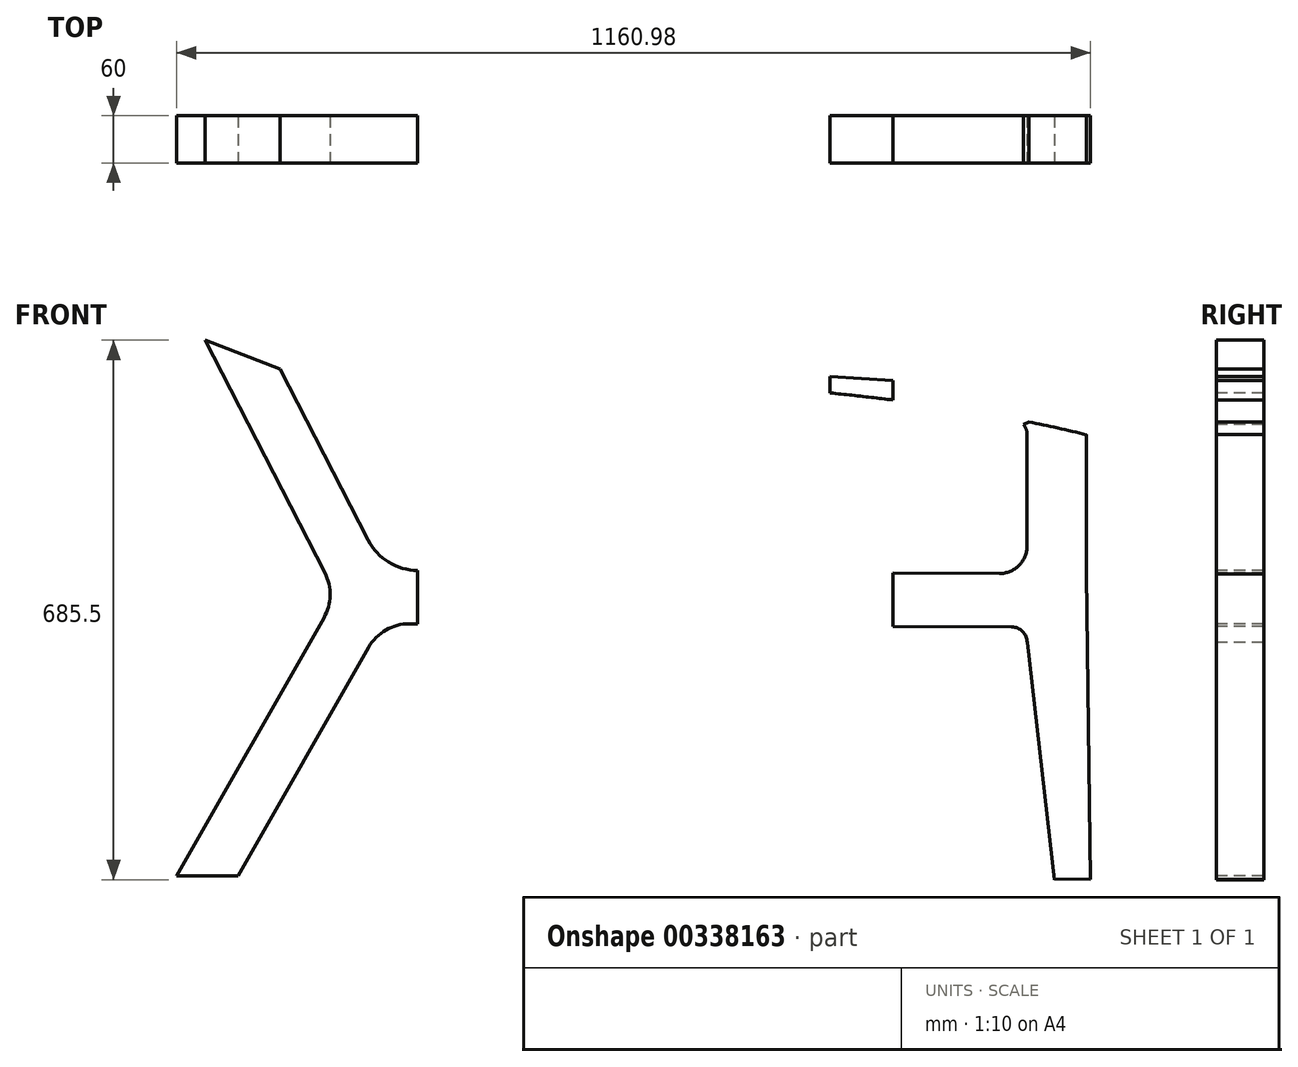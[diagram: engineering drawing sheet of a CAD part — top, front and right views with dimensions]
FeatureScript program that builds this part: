
annotation { "Feature Type Name" : "Feature", "Feature Type Description" : "" }
export const myFeature = defineFeature(function(context is Context, id is Id, definition is map)
    precondition{}
    {
        {
            var Q0;
            Q0=qCreatedBy(makeId("Front.planeOp"),FACE);
            var sketch = newSketch(context, id + "F0", { "sketchPlane" : qUnion([Q0])});
            skLineSegment(sketch, "E0.left", {"start": v(787.99, 506.8) * mm, "end": v(792.91, 118.96) * mm});
            skPoint(sketch, "E0.middle", {"position": v(0, 0) * mm});
            skLineSegment(sketch, "E1", {"start": v(-180.83, 451.22) * mm, "end": v(-368.07, 123.56) * mm});
            skLineSegment(sketch, "E2", {"start": v(-332.03, 803.88) * mm, "end": v(-179.6, 507.98) * mm});
            skLineSegment(sketch, "E3.0", {"start": v(-124.03, 413.58) * mm, "end": v(-289.76, 123.56) * mm});
            skArc(sketch, "E4.filletArc", {"start": v(-180.83, 451.22) * mm, "mid": v(-173, 479.45) * mm, "end": v(-179.6, 507.98) * mm});
            skLineSegment(sketch, "E5.0", {"start": v(677.16, 507.4) * mm, "end": v(-61.91, 511.32) * mm});
            skLineSegment(sketch, "E6.0", {"start": v(692.7, 439.5) * mm, "end": v(-72.06, 443.56) * mm});
            skArc(sketch, "E7.filletArc", {"start": v(-124.66, 549.81) * mm, "mid": v(-98.67, 521.8) * mm, "end": v(-61.91, 511.32) * mm});
            skArc(sketch, "E8.filletArc", {"start": v(-72.06, 443.56) * mm, "mid": v(-102.1, 435.6) * mm, "end": v(-124.03, 413.58) * mm});
            skLineSegment(sketch, "E9", {"start": v(787.99, 506.8) * mm, "end": v(787.99, 727.43) * mm});
            skLineSegment(sketch, "E10", {"start": v(778.63, 737.4) * mm, "end": v(-255.55, 803.88) * mm});
            skPoint(sketch, "E11.visualSharp", {"position": v(787.99, 736.8) * mm});
            skArc(sketch, "E11.filletArc", {"start": v(787.99, 727.43) * mm, "mid": v(785.28, 734.27) * mm, "end": v(778.63, 737.4) * mm});
            skLineSegment(sketch, "E12", {"start": v(712.35, 542.4) * mm, "end": v(712.35, 684.08) * mm});
            skFitSpline(sketch, "E13", {"points": [v(-236.6, 767.12) * mm, v(712.35, 700.53) * mm, v(1259.08, 515) * mm], "startDerivative": vector(1811.82, -32.7) * mm, "endDerivative": vector(1152.25, -490.48) * mm});
            skArc(sketch, "E14.filletArc", {"start": v(712.35, 684.08) * mm, "mid": v(707.77, 696.81) * mm, "end": v(696.12, 703.72) * mm});
            skLineSegment(sketch, "E15", {"start": v(-289.76, 123.56) * mm, "end": v(-368.07, 123.56) * mm});
            skLineSegment(sketch, "E16", {"start": v(746.82, 119.2) * mm, "end": v(792.91, 118.96) * mm});
            skPoint(sketch, "E17.orphan", {"position": v(717.96, -2.77) * mm});
            skArc(sketch, "E18.filletArc", {"start": v(677.16, 507.4) * mm, "mid": v(702.03, 517.58) * mm, "end": v(712.35, 542.4) * mm});
            skPoint(sketch, "E19.visualSharp", {"position": v(712.35, 439.4) * mm});
            skArc(sketch, "E19.filletArc", {"start": v(712.6, 419.75) * mm, "mid": v(706.69, 433.7) * mm, "end": v(692.7, 439.5) * mm});
            skFitSpline(sketch, "E20", {"points": [v(-255.55, 803.88) * mm, v(-332.03, 803.88) * mm, v(-587.75, 764.2) * mm], "startDerivative": vector(-185.9, 10.78) * mm, "endDerivative": vector(-452.25, -81.08) * mm});
            skLineSegment(sketch, "E21.trimOffspring", {"start": v(-236.6, 767.12) * mm, "end": v(-124.66, 549.81) * mm});
            skLineSegment(sketch, "E22", {"start": v(-332.03, 803.88) * mm, "end": v(-236.6, 767.12) * mm});
            skLineSegment(sketch, "E23.0", {"start": v(746.9, 119.2) * mm, "end": v(746.92, 118.38) * mm});
            skLineSegment(sketch, "E24", {"start": v(712.6, 419.75) * mm, "end": v(746.92, 118.38) * mm});
            skPoint(sketch, "E25.start.orphan", {"position": v(785.28, 734.27) * mm});
            skLineSegment(sketch, "E26", {"start": v(785.28, 734.27) * mm, "end": v(707.77, 696.81) * mm});
            skLineSegment(sketch, "E27", {"start": v(-61.91, 511.32) * mm, "end": v(-61.91, 443.5) * mm});
            skLineSegment(sketch, "E28", {"start": v(-61.91, 477.41) * mm, "end": v(542, 477.41) * mm});
            skLineSegment(sketch, "E29", {"start": v(542, 477.41) * mm, "end": v(542, 55.83) * mm});
            skLineSegment(sketch, "E30", {"start": v(542, 477.41) * mm, "end": v(542, 816.93) * mm});
            skLineSegment(sketch, "E31.0", {"start": v(462, 477.41) * mm, "end": v(462, 55.83) * mm});
            skLineSegment(sketch, "E31.1", {"start": v(462, 477.41) * mm, "end": v(462, 816.93) * mm});
            skSolve(sketch);
        }
        {
            var Q0;
            {var subQ3=sQuery(id+"F0.wireOp",EDGE,"E23.0");Q0=makeQuery(id+"F0.imprint","IMPRINT",FACE,{"disambiguationData":[TD([[makeQuery(id+"F0.imprint","IMPRINT",EDGE,{"derivedFrom":subQ3}),-1.0]])]});}
            var Q1;
            Q1=makeQuery(id+"F0.imprint","IMPRINT",FACE,{"disambiguationData":[TD([[makeQuery(id+"F0.imprint","IMPRINT",EDGE,{"derivedFrom":sQuery(id+"F0.wireOp",EDGE,"E1")}),1.0]])]});
            var Q2;
            {var subQ4=sQuery(id+"F0.wireOp",EDGE,"E10");Q2=makeQuery(id+"F0.imprint","IMPRINT",FACE,{"disambiguationData":[TD([[makeQuery(id+"F0.imprint","IMPRINT",EDGE,{"derivedFrom":subQ4}),1.0]])]});}
            var Q3;
            {var subQ1=sQuery(id+"F0.wireOp",EDGE,"E0.left");Q3=makeQuery(id+"F0.imprint","IMPRINT",FACE,{"disambiguationData":[TD([[makeQuery(id+"F0.imprint","IMPRINT",EDGE,{"derivedFrom":subQ1}),-1.0]])]});}
            extrude(context, id + "F1", {"entities" : qUnion([Q0, Q1, Q2, Q3]), "endBound" : BoundingType.SYMMETRIC, "oppositeDirection" : true, "depth" : 60 * mm});
        }
    });
